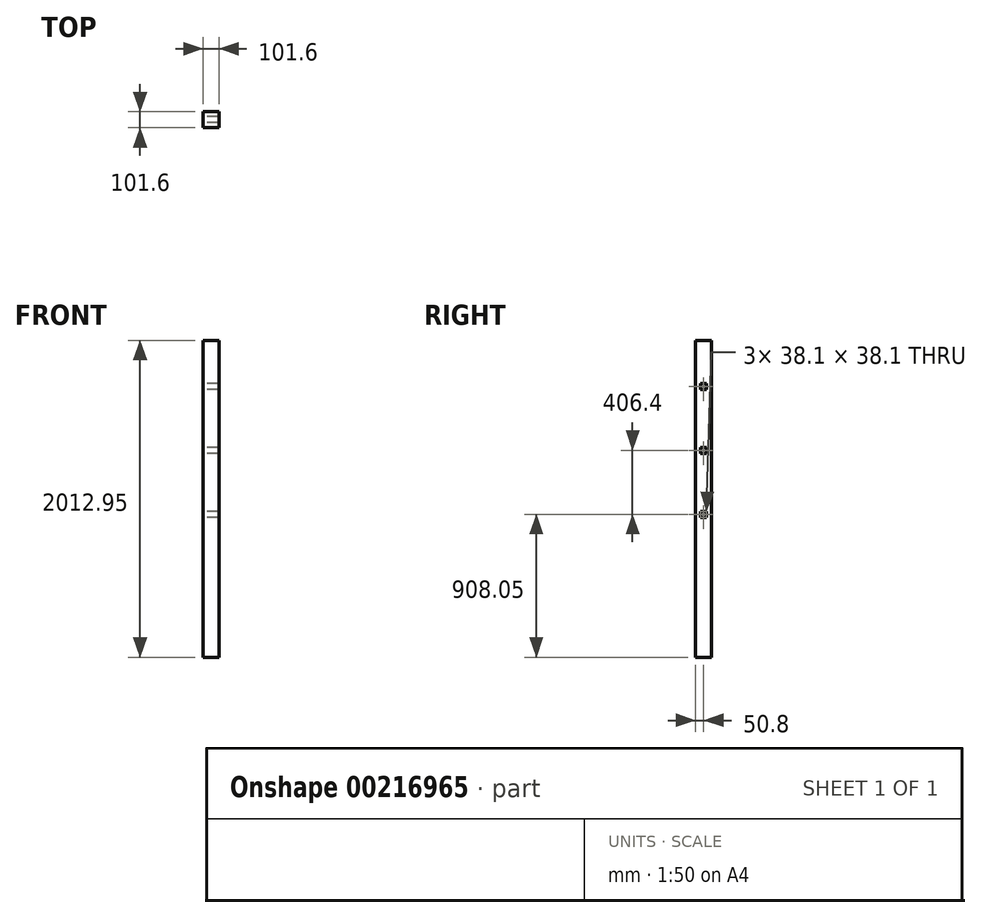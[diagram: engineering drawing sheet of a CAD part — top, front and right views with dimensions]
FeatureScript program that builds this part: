
annotation { "Feature Type Name" : "Feature", "Feature Type Description" : "" }
export const myFeature = defineFeature(function(context is Context, id is Id, definition is map)
    precondition{}
    {
        {
            var Q0;
            Q0=qCreatedBy(makeId("Right.planeOp"), FACE);
            var sketch = newSketch(context, id + "F0", { "sketchPlane" : qUnion([Q0])});
            skLineSegment(sketch, "E0.bottom", {"start": v(-101.6, 2012.95) * mm, "end": v(0, 2012.95) * mm});
            skLineSegment(sketch, "E0.top", {"start": v(-101.6, 0) * mm, "end": v(0, 0) * mm});
            skLineSegment(sketch, "E0.left", {"start": v(-101.6, 2012.95) * mm, "end": v(-101.6, 0) * mm});
            skLineSegment(sketch, "E0.right", {"start": v(0, 2012.95) * mm, "end": v(0, 0) * mm});
            skLineSegment(sketch, "E1.bottom", {"start": v(-69.85, 1739.9) * mm, "end": v(-31.75, 1739.9) * mm});
            skLineSegment(sketch, "E1.top", {"start": v(-69.85, 1701.8) * mm, "end": v(-31.75, 1701.8) * mm});
            skLineSegment(sketch, "E1.left", {"start": v(-69.85, 1739.9) * mm, "end": v(-69.85, 1701.8) * mm});
            skLineSegment(sketch, "E1.right", {"start": v(-31.75, 1739.9) * mm, "end": v(-31.75, 1701.8) * mm});
            skLineSegment(sketch, "E2.bottom", {"start": v(-69.85, 1333.5) * mm, "end": v(-31.75, 1333.5) * mm});
            skLineSegment(sketch, "E2.top", {"start": v(-69.85, 1295.4) * mm, "end": v(-31.75, 1295.4) * mm});
            skLineSegment(sketch, "E2.left", {"start": v(-69.85, 1333.5) * mm, "end": v(-69.85, 1295.4) * mm});
            skLineSegment(sketch, "E2.right", {"start": v(-31.75, 1333.5) * mm, "end": v(-31.75, 1295.4) * mm});
            skLineSegment(sketch, "E3.bottom", {"start": v(-69.85, 927.1) * mm, "end": v(-31.75, 927.1) * mm});
            skLineSegment(sketch, "E3.top", {"start": v(-69.85, 889) * mm, "end": v(-31.75, 889) * mm});
            skLineSegment(sketch, "E3.left", {"start": v(-69.85, 927.1) * mm, "end": v(-69.85, 889) * mm});
            skLineSegment(sketch, "E3.right", {"start": v(-31.75, 927.1) * mm, "end": v(-31.75, 889) * mm});
            skSolve(sketch);
        }
        {
            var Q0;
            Q0 = qSketchRegion(id + "F0", true);
            extrude(context, id + "F1", {"entities" : qUnion([Q0]), "domain" : OperationDomain.MODEL, "flatOperationType" : FlatOperationType.REMOVE, "depth" : 101.6 * mm, "offsetDistance" : 25.4 * mm});
        }
    });
